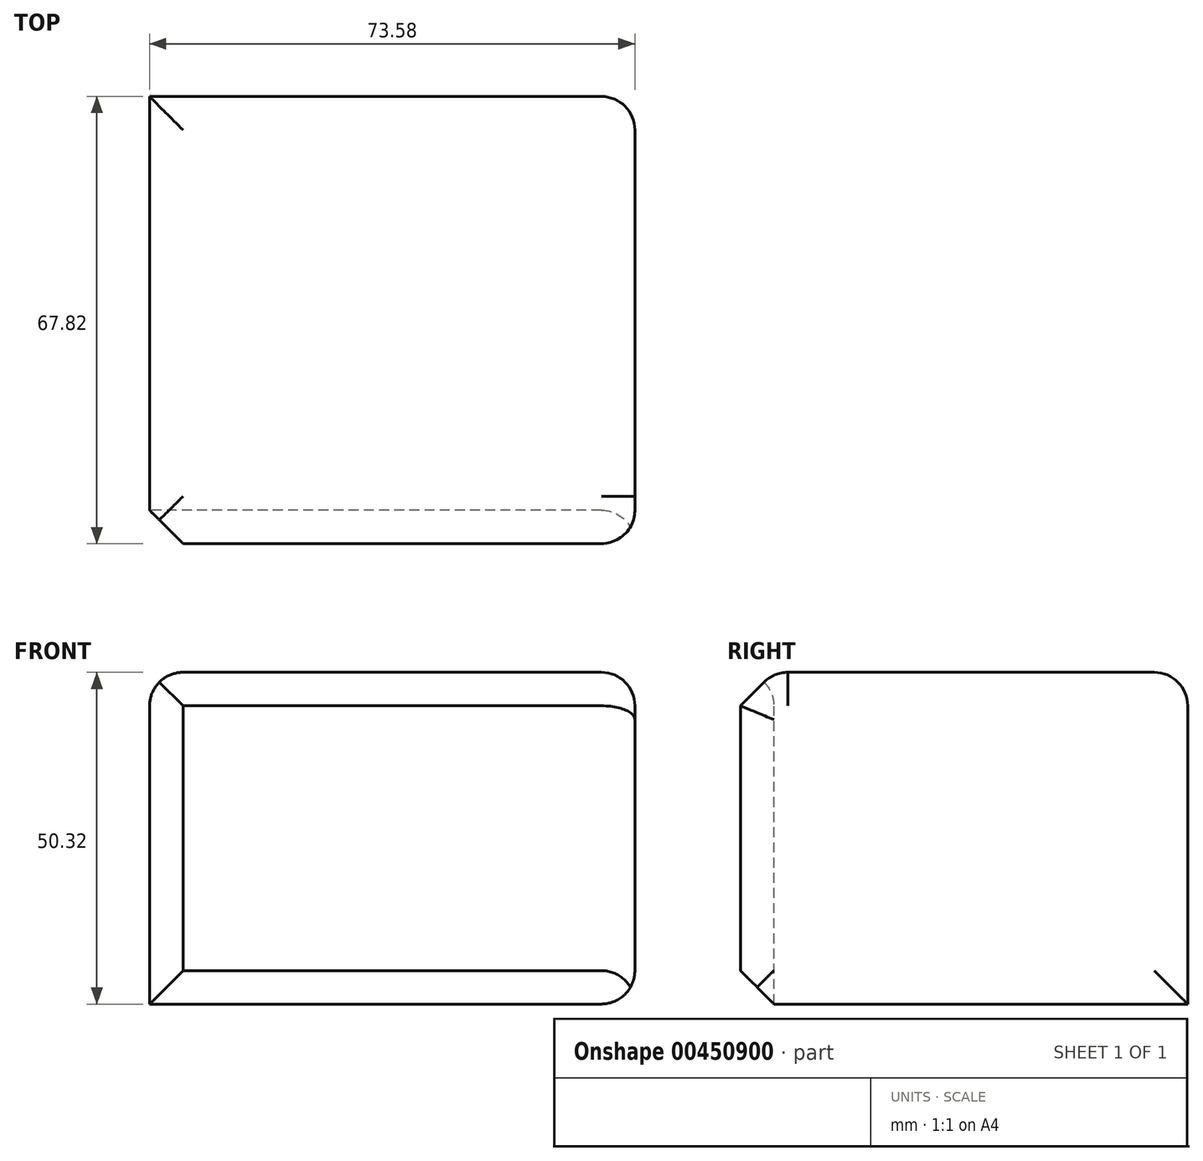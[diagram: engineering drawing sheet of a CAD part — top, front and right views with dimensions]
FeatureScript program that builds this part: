
annotation { "Feature Type Name" : "Feature", "Feature Type Description" : "" }
export const myFeature = defineFeature(function(context is Context, id is Id, definition is map)
    precondition{}
    {
        {
            var Q0;
            Q0=qCreatedBy(makeId("Front.planeOp"),FACE);
            var sketch = newSketch(context, id + "F0", { "sketchPlane" : qUnion([Q0])});
            skLineSegment(sketch, "E0.bottom", {"start": v(-56.5, 45.69) * mm, "end": v(17.1, 45.69) * mm});
            skLineSegment(sketch, "E0.top", {"start": v(-56.5, -4.63) * mm, "end": v(17.1, -4.63) * mm});
            skLineSegment(sketch, "E0.left", {"start": v(-56.5, 45.69) * mm, "end": v(-56.5, -4.63) * mm});
            skLineSegment(sketch, "E0.right", {"start": v(17.1, 45.69) * mm, "end": v(17.1, -4.63) * mm});
            skSolve(sketch);
        }
        {
            var Q0;
            Q0 = qSketchRegion(id + "F0", true);
            extrude(context, id + "F1", {"entities" : qUnion([Q0]), "depth" : 67.82 * mm});
        }
        {
            var Q0;
            Q0=makeQuery(id+"F1.opExtrude","CAP_EDGE",EDGE,{"disambiguationData":[OSD([sQuery(id+"F0.wireOp",EDGE,"E0.right")])],"isStart":false});
            var Q1;
            Q1=makeQuery(id+"F1.opExtrude","SWEPT_EDGE",EDGE,{"disambiguationData":[OSD([sQuery(id+"F0.wireOp",EDGE,"E0.bottom"),sQuery(id+"F0.wireOp",EDGE,"E0.right")])]});
            var Q2;
            Q2=makeQuery(id+"F1.opExtrude","SWEPT_FACE",FACE,{"disambiguationData":[OSD([sQuery(id+"F0.wireOp",EDGE,"E0.right")])]});
            fillet(context, id + "F2", {"entities" : qUnion([Q0, Q1, Q2]), "radius" : 5.08 * mm, "tangentPropagation" : true, "allowEdgeOverflow" : false});
        }
        {
            var Q0;
            Q0=makeQuery(id+"F1.opExtrude","CAP_FACE",FACE,{"disambiguationData":[OSD([sQuery(id+"F0.wireOp",EDGE,"E0.bottom"),sQuery(id+"F0.wireOp",EDGE,"E0.top"),sQuery(id+"F0.wireOp",EDGE,"E0.left"),sQuery(id+"F0.wireOp",EDGE,"E0.right")])],"isStart":false});
            chamfer(context, id + "F3", {"entities" : qUnion([Q0]), "width" : 5.08 * mm, "tangentPropagation" : true});
        }
        {
            var Q0;
            Q0=makeQuery(id+"F1.opExtrude","SWEPT_FACE",FACE,{"disambiguationData":[OSD([sQuery(id+"F0.wireOp",EDGE,"E0.bottom")])]});
            fillet(context, id + "F4", {"entities" : qUnion([Q0]), "radius" : 5.08 * mm, "tangentPropagation" : true, "allowEdgeOverflow" : false});
        }
    });
